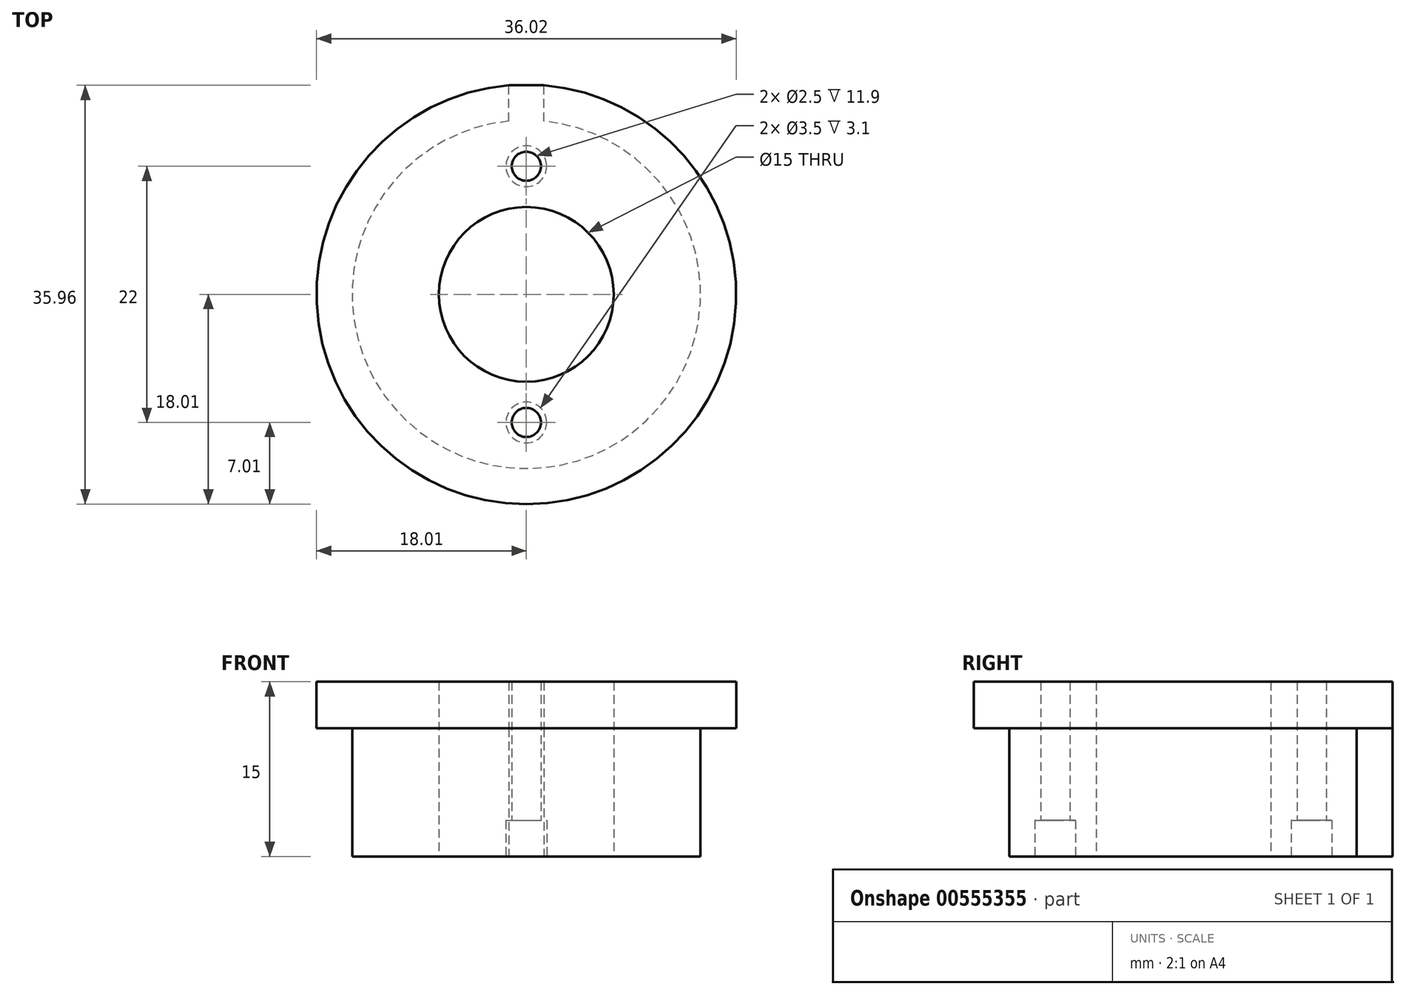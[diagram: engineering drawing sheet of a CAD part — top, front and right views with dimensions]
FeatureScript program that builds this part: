
annotation { "Feature Type Name" : "Feature", "Feature Type Description" : "" }
export const myFeature = defineFeature(function(context is Context, id is Id, definition is map)
    precondition{}
    {
        {
            var Q0;
            Q0=qCreatedBy(makeId("Top.planeOp"),FACE);
            var sketch = newSketch(context, id + "F0", { "sketchPlane" : qUnion([Q0])});
            skArc(sketch, "E0", {"start": v(-1.5, 14.87) * mm, "mid": v(0, -14.95) * mm, "end": v(1.5, 14.87) * mm});
            skLineSegment(sketch, "E1.top", {"start": v(1.5, 17.95) * mm, "end": v(-1.5, 17.95) * mm});
            skLineSegment(sketch, "E1.left", {"start": v(1.5, 14.87) * mm, "end": v(1.5, 17.95) * mm});
            skLineSegment(sketch, "E1.right", {"start": v(-1.5, 14.87) * mm, "end": v(-1.5, 17.95) * mm});
            skPoint(sketch, "E1.middle", {"position": v(0, 14.95) * mm});
            skPoint(sketch, "E2.orphan", {"position": v(-1.5, 11.95) * mm});
            skPoint(sketch, "E3.orphan", {"position": v(1.5, 11.95) * mm});
            skSolve(sketch);
        }
        {
            var Q0;
            Q0 = qSketchRegion(id + "F0", true);
            extrude(context, id + "F1", {"entities" : qUnion([Q0]), "depth" : 11 * mm, "offsetDistance" : 25 * mm});
        }
        {
            var Q0;
            Q0=makeQuery(id+"F1.opExtrude","CAP_FACE",FACE,{"disambiguationData":[OSD([sQuery(id+"F0.wireOp",EDGE,"E0"),sQuery(id+"F0.wireOp",EDGE,"E1.top"),sQuery(id+"F0.wireOp",EDGE,"E1.left"),sQuery(id+"F0.wireOp",EDGE,"E1.right")])],"isStart":false});
            var sketch = newSketch(context, id + "F2", { "sketchPlane" : qUnion([Q0])});
            skCircle(sketch, "E4", {"center": v(0, 0) * mm, "radius": 18.01 * mm});
            skSolve(sketch);
        }
        {
            var Q0;
            Q0=makeQuery(id+"F2.imprint","IMPRINT",FACE,{"disambiguationData":[TD([[makeQuery(id+"F2.imprint","IMPRINT",EDGE,{"derivedFrom":makeQuery(id+"F1.opExtrude","CAP_EDGE",EDGE,{"disambiguationData":[OSD([sQuery(id+"F0.wireOp",EDGE,"E0")])],"isStart":false})}),-1.0]])]});
            var Q1;
            Q1=makeQuery(id+"F2.imprint","IMPRINT",FACE,{"disambiguationData":[TD([[makeQuery(id+"F2.imprint","IMPRINT",EDGE,{"derivedFrom":makeQuery(id+"F1.opExtrude","CAP_EDGE",EDGE,{"disambiguationData":[OSD([sQuery(id+"F0.wireOp",EDGE,"E0")])],"isStart":false})}),1.0]])]});
            extrude(context, id + "F3", {"entities" : qUnion([Q0, Q1]), "operationType" : NewBodyOperationType.ADD, "depth" : 4 * mm, "offsetDistance" : 25 * mm});
        }
        {
            var Q0;
            Q0=makeQuery(id+"F1.opExtrude","CAP_FACE",FACE,{"disambiguationData":[OSD([sQuery(id+"F0.wireOp",EDGE,"E0"),sQuery(id+"F0.wireOp",EDGE,"E1.top"),sQuery(id+"F0.wireOp",EDGE,"E1.left"),sQuery(id+"F0.wireOp",EDGE,"E1.right")])],"isStart":true});
            var sketch = newSketch(context, id + "F4", { "sketchPlane" : qUnion([Q0])});
            skCircle(sketch, "E5", {"center": v(0, 0) * mm, "radius": 7.5 * mm});
            skSolve(sketch);
        }
        {
            var Q0;
            Q0=makeQuery(id+"F4.imprint","IMPRINT",FACE,{"disambiguationData":[TD([[makeQuery(id+"F4.imprint","IMPRINT",EDGE,{"derivedFrom":sQuery(id+"F4.wireOp",EDGE,"E5")}),1.0]])]});
            extrude(context, id + "F5", {"entities" : qUnion([Q0]), "operationType" : NewBodyOperationType.REMOVE, "oppositeDirection" : true, "depth" : 25 * mm, "offsetDistance" : 25 * mm});
        }
        {
            var Q0;
            Q0=makeQuery(id+"F1.opExtrude","CAP_FACE",FACE,{"disambiguationData":[OSD([sQuery(id+"F0.wireOp",EDGE,"E0"),sQuery(id+"F0.wireOp",EDGE,"E1.top"),sQuery(id+"F0.wireOp",EDGE,"E1.left"),sQuery(id+"F0.wireOp",EDGE,"E1.right")])],"isStart":true});
            var sketch = newSketch(context, id + "F6", { "sketchPlane" : qUnion([Q0])});
            skLineSegment(sketch, "E6", {"start": v(0, 0) * mm, "end": v(0, 11) * mm, "construction": true});
            skLineSegment(sketch, "E7", {"start": v(0, 0) * mm, "end": v(0, -11) * mm, "construction": true});
            skCircle(sketch, "E8", {"center": v(0, 11) * mm, "radius": 1.25 * mm});
            skCircle(sketch, "E9", {"center": v(0, -11) * mm, "radius": 1.25 * mm});
            skCircle(sketch, "E10", {"center": v(0, 11) * mm, "radius": 1.75 * mm});
            skCircle(sketch, "E11", {"center": v(0, -11) * mm, "radius": 1.75 * mm});
            skSolve(sketch);
        }
        {
            var Q0;
            Q0=makeQuery(id+"F6.imprint","IMPRINT",FACE,{"disambiguationData":[TD([[makeQuery(id+"F6.imprint","IMPRINT",EDGE,{"derivedFrom":sQuery(id+"F6.wireOp",EDGE,"E9")}),1.0]])]});
            var Q1;
            Q1=makeQuery(id+"F6.imprint","IMPRINT",FACE,{"disambiguationData":[TD([[makeQuery(id+"F6.imprint","IMPRINT",EDGE,{"derivedFrom":sQuery(id+"F6.wireOp",EDGE,"E8")}),1.0]])]});
            extrude(context, id + "F7", {"entities" : qUnion([Q0, Q1]), "operationType" : NewBodyOperationType.REMOVE, "oppositeDirection" : true, "depth" : 25 * mm, "offsetDistance" : 25 * mm});
        }
        {
            var Q0;
            Q0=makeQuery(id+"F6.imprint","IMPRINT",FACE,{"disambiguationData":[TD([[makeQuery(id+"F6.imprint","IMPRINT",EDGE,{"derivedFrom":sQuery(id+"F6.wireOp",EDGE,"E8")}),-1.0]])]});
            var Q1;
            Q1=makeQuery(id+"F6.imprint","IMPRINT",FACE,{"disambiguationData":[TD([[makeQuery(id+"F6.imprint","IMPRINT",EDGE,{"derivedFrom":sQuery(id+"F6.wireOp",EDGE,"E9")}),-1.0]])]});
            extrude(context, id + "F8", {"entities" : qUnion([Q0, Q1]), "operationType" : NewBodyOperationType.REMOVE, "oppositeDirection" : true, "depth" : 3.1 * mm, "offsetDistance" : 25 * mm});
        }
    });
